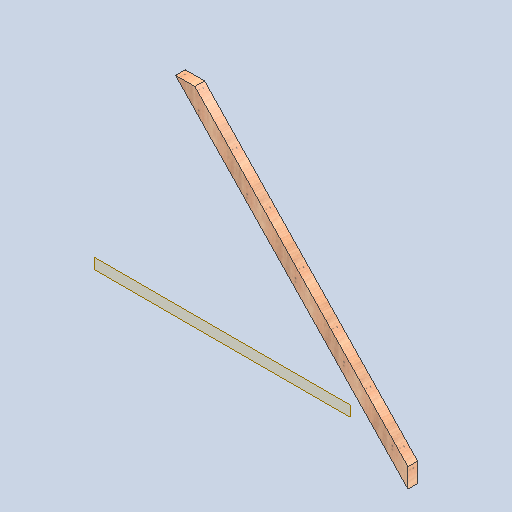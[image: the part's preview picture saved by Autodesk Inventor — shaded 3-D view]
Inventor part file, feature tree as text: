
AUTODESK INVENTOR PART (.ipt)
format: ipt  version: 2025 (Build 290162000, 162)  size: 145,408 bytes
history: native  units: in
note: dims shown in document units (in); Inventor stores cm internally (conversion verified against a paired STEP export)
features: other x5, reference x3, plane x1, extrude x1, sketch x1
ambient origin geometry x8: Origin, YZ Plane, XZ Plane, XY Plane, X Axis, Y Axis, Z Axis, Center Point
bodies: Body1 (feature_tree)
feature tree (11):
  plane  "Work Plane1"
  extrude  "Extrusion3"  Depth=2.0in TaperAngle=0.0deg
  sketch  "Sketch1"  dims[d5=4.0in d6=2.0in d7=0.0in]
  reference  "Reference1"
  reference  "Reference2"
  reference  "Reference3"
  other  "<userpath>\Documents\GitHub\USCTigerBurn24\v2\Tiger.iam"
  other  "Tiger.iam"
  other  "2x4x48:14"
  other  "2x4x48:12"
  other  "2x4x48:9"
